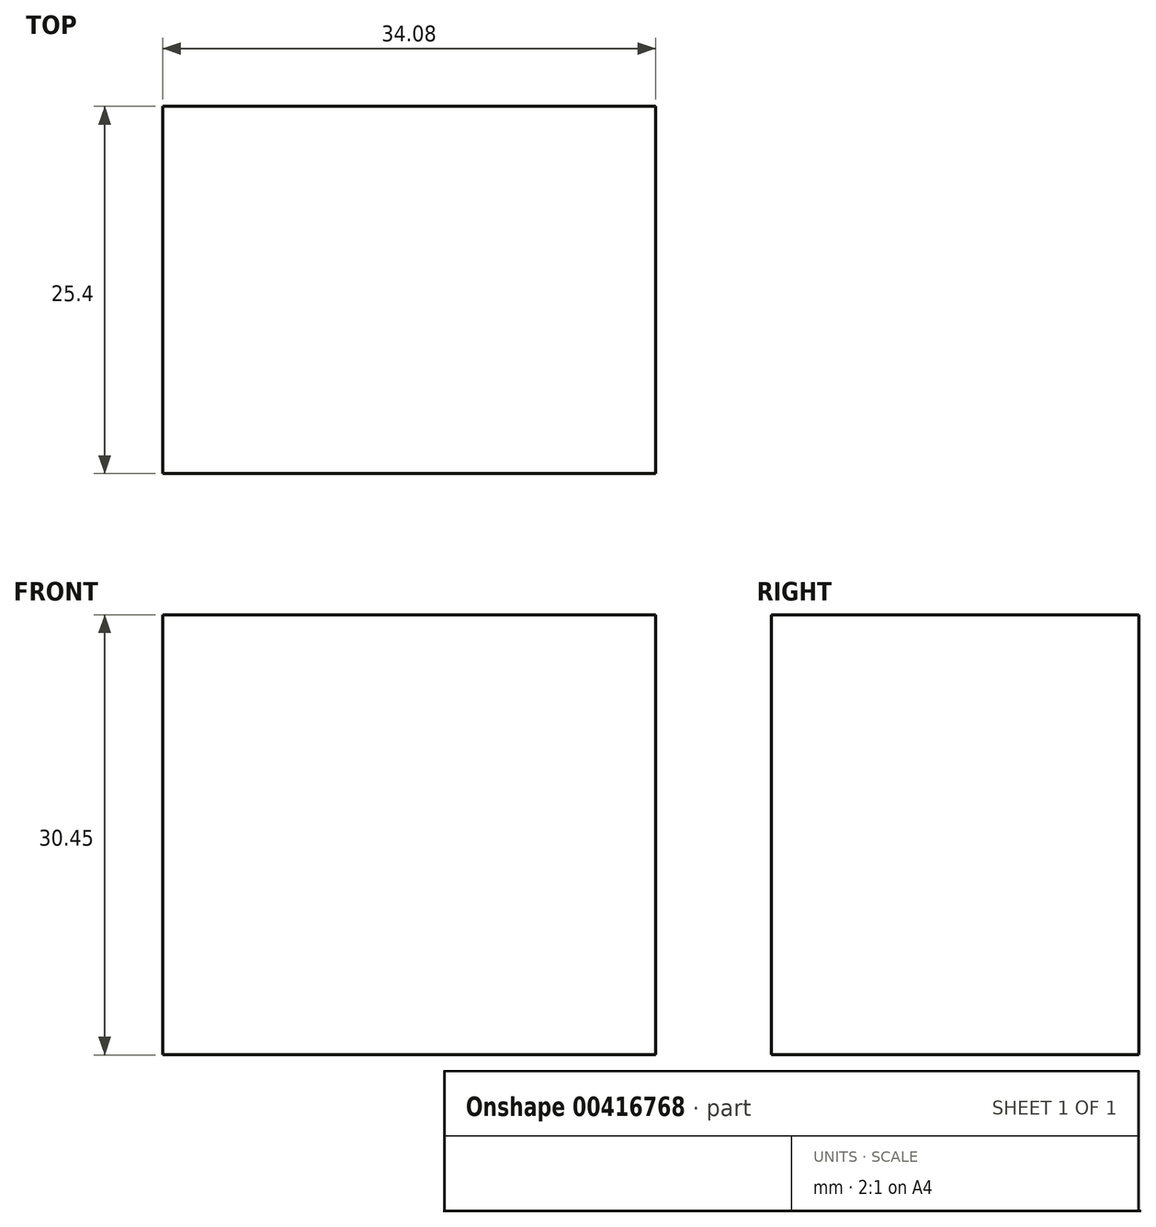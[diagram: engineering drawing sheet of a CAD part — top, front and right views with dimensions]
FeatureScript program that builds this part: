
annotation { "Feature Type Name" : "Feature", "Feature Type Description" : "" }
export const myFeature = defineFeature(function(context is Context, id is Id, definition is map)
    precondition{}
    {
        {
            var Q0;
            Q0=qCreatedBy(makeId("Front.planeOp"),FACE);
            var sketch = newSketch(context, id + "F0", { "sketchPlane" : qUnion([Q0])});
            skLineSegment(sketch, "E0.bottom", {"start": v(-106.51, 38.78) * mm, "end": v(-72.43, 38.78) * mm});
            skLineSegment(sketch, "E0.top", {"start": v(-106.51, 8.33) * mm, "end": v(-72.43, 8.33) * mm});
            skLineSegment(sketch, "E0.left", {"start": v(-106.51, 38.78) * mm, "end": v(-106.51, 8.33) * mm});
            skLineSegment(sketch, "E0.right", {"start": v(-72.43, 38.78) * mm, "end": v(-72.43, 8.33) * mm});
            skSolve(sketch);
        }
        {
            var Q0;
            Q0 = qSketchRegion(id + "F0", true);
            extrude(context, id + "F1", {"entities" : qUnion([Q0]), "depth" : 25.4 * mm});
        }
    });
